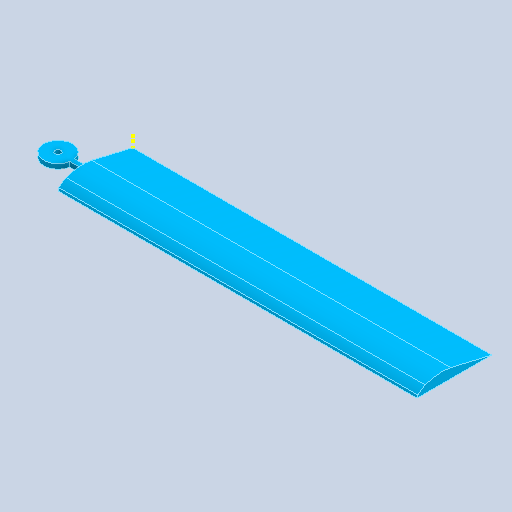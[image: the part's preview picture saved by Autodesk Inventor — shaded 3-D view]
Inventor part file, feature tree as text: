
AUTODESK INVENTOR PART (.ipt)
format: ipt  version: 2023 (Build 270158000, 158)  size: 109,056 bytes
history: native  units: mm
features: sketch x8, other x3
ambient origin geometry x8: Origin, YZ Plane, XZ Plane, XY Plane, X Axis, Y Axis, Z Axis, Center Point
bodies: Solid1 (feature_tree)
feature tree (11):
  other  "R wing.ipt"
  other  "Solid1::R wing.ipt"
  other  "TaggingFeature1"
  sketch  "Sketch1"  dims[d0=10.0mm]
  sketch  "Sketch2"
  sketch  "Sketch3"
  sketch  "Sketch4"
  sketch  "Sketch5"
  sketch  "Sketch6"
  sketch  "Sketch7"
  sketch  "Sketch8"
